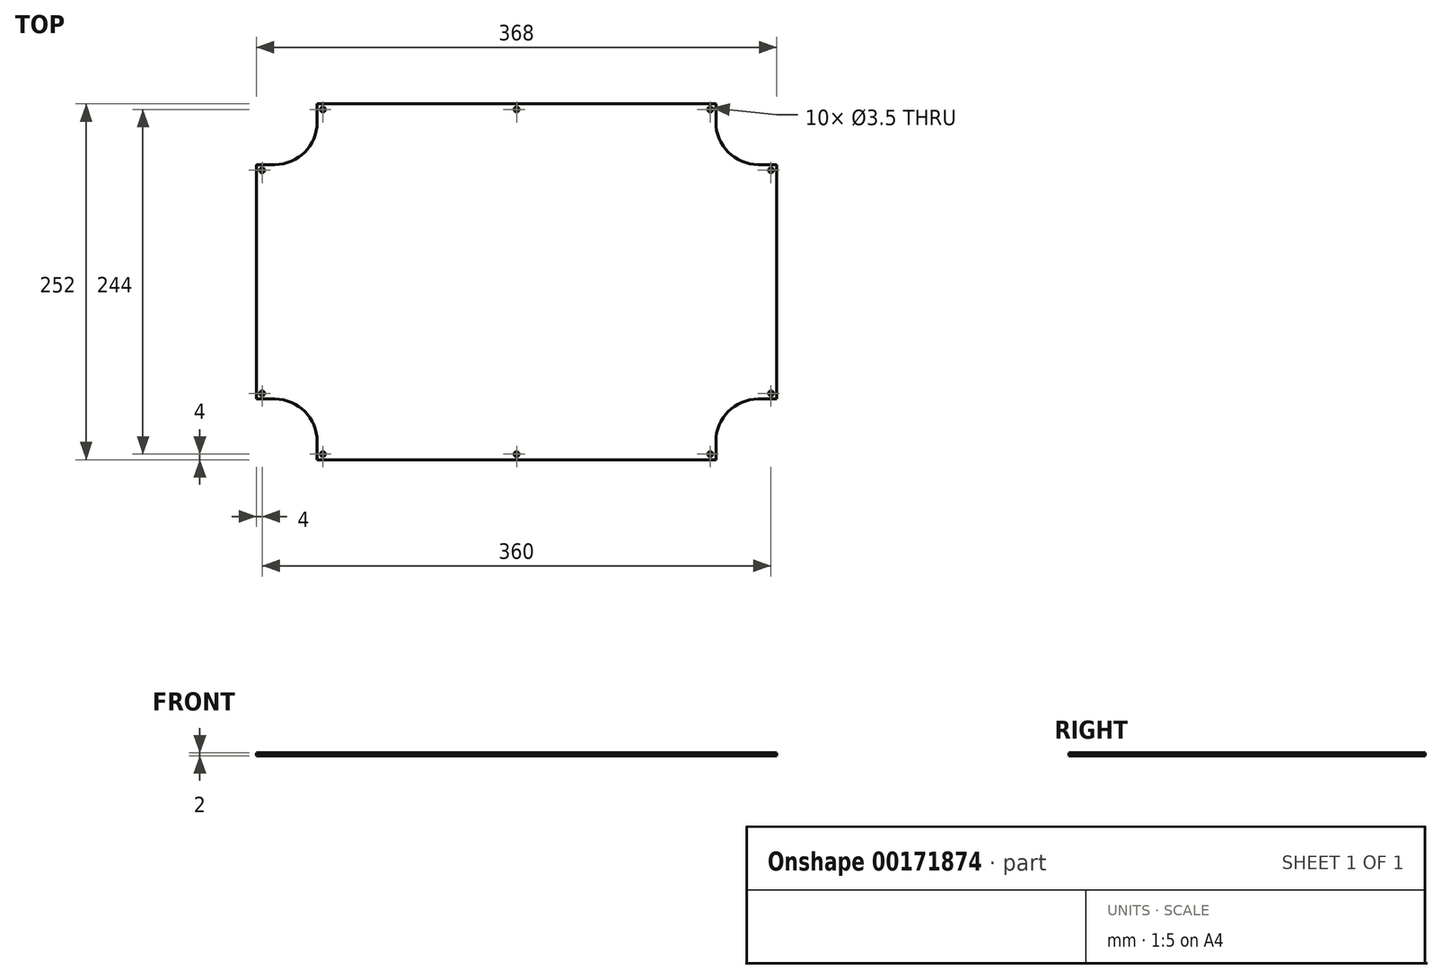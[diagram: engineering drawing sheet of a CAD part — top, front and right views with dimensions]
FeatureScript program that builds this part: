
annotation { "Feature Type Name" : "Feature", "Feature Type Description" : "" }
export const myFeature = defineFeature(function(context is Context, id is Id, definition is map)
    precondition{}
    {
        {
            var Q0;
            Q0=qCreatedBy(makeId("Top.planeOp"),FACE);
            var sketch = newSketch(context, id + "F0", { "sketchPlane" : qUnion([Q0])});
            skLineSegment(sketch, "E0", {"start": v(-141, 126) * mm, "end": v(141, 126) * mm});
            skLineSegment(sketch, "E1", {"start": v(141, 126) * mm, "end": v(141, 113) * mm});
            skLineSegment(sketch, "E2", {"start": v(171, 83) * mm, "end": v(184, 83) * mm});
            skLineSegment(sketch, "E3", {"start": v(184, 83) * mm, "end": v(184, -83) * mm});
            skLineSegment(sketch, "E4", {"start": v(184, -83) * mm, "end": v(171, -83) * mm});
            skLineSegment(sketch, "E5", {"start": v(141, -113) * mm, "end": v(141, -126) * mm});
            skLineSegment(sketch, "E6", {"start": v(141, -126) * mm, "end": v(-141, -126) * mm});
            skLineSegment(sketch, "E7", {"start": v(-141, -126) * mm, "end": v(-141, -113) * mm});
            skLineSegment(sketch, "E8", {"start": v(-171, -83) * mm, "end": v(-184, -83) * mm});
            skLineSegment(sketch, "E9", {"start": v(-184, -83) * mm, "end": v(-184, 83) * mm});
            skLineSegment(sketch, "E10", {"start": v(-184, 83) * mm, "end": v(-171, 83) * mm});
            skLineSegment(sketch, "E11", {"start": v(-141, 113) * mm, "end": v(-141, 126) * mm});
            skPoint(sketch, "E12.visualSharp", {"position": v(-141, 83) * mm});
            skArc(sketch, "E12.filletArc", {"start": v(-171, 83) * mm, "mid": v(-149.79, 91.79) * mm, "end": v(-141, 113) * mm});
            skPoint(sketch, "E13.visualSharp", {"position": v(141, 83) * mm});
            skArc(sketch, "E13.filletArc", {"start": v(141, 113) * mm, "mid": v(149.79, 91.79) * mm, "end": v(171, 83) * mm});
            skPoint(sketch, "E14.visualSharp", {"position": v(141, -83) * mm});
            skArc(sketch, "E14.filletArc", {"start": v(171, -83) * mm, "mid": v(149.79, -91.79) * mm, "end": v(141, -113) * mm});
            skPoint(sketch, "E15.visualSharp", {"position": v(-141, -83) * mm});
            skArc(sketch, "E15.filletArc", {"start": v(-141, -113) * mm, "mid": v(-149.79, -91.79) * mm, "end": v(-171, -83) * mm});
            skPoint(sketch, "E16", {"position": v(0, 126) * mm});
            skPoint(sketch, "E17", {"position": v(0, -126) * mm});
            skPoint(sketch, "E18", {"position": v(-184, 0) * mm});
            skPoint(sketch, "E19", {"position": v(184, 0) * mm});
            skLineSegment(sketch, "E20", {"start": v(-137, 139.15) * mm, "end": v(-137, -174.05) * mm, "construction": true});
            skLineSegment(sketch, "E21", {"start": v(-207.28, 122) * mm, "end": v(169.12, 122) * mm, "construction": true});
            skLineSegment(sketch, "E22", {"start": v(-202.37, 79) * mm, "end": v(209.85, 79) * mm, "construction": true});
            skLineSegment(sketch, "E23.MirrorCS", {"start": v(-202.37, -79) * mm, "end": v(209.85, -79) * mm, "construction": true});
            skLineSegment(sketch, "E24.MirrorCS", {"start": v(-207.28, -122) * mm, "end": v(169.12, -122) * mm, "construction": true});
            skLineSegment(sketch, "E25.MirrorCS", {"start": v(137, 139.15) * mm, "end": v(137, -174.05) * mm, "construction": true});
            skLineSegment(sketch, "E26", {"start": v(-180, 93.5) * mm, "end": v(-180, -106.64) * mm, "construction": true});
            skLineSegment(sketch, "E27.MirrorCS", {"start": v(180, 93.5) * mm, "end": v(180, -106.64) * mm, "construction": true});
            skLineSegment(sketch, "E28", {"start": v(0, 134.08) * mm, "end": v(0, -140) * mm, "construction": true});
            skCircle(sketch, "E29", {"center": v(0, 122) * mm, "radius": 1.75 * mm});
            skCircle(sketch, "E30", {"center": v(-137, 122) * mm, "radius": 1.75 * mm});
            skCircle(sketch, "E31", {"center": v(137, 122) * mm, "radius": 1.75 * mm});
            skCircle(sketch, "E32", {"center": v(-180, 79) * mm, "radius": 1.75 * mm});
            skCircle(sketch, "E33", {"center": v(-180, -79) * mm, "radius": 1.75 * mm});
            skCircle(sketch, "E34", {"center": v(-137, -122) * mm, "radius": 1.75 * mm});
            skCircle(sketch, "E35", {"center": v(0, -122) * mm, "radius": 1.75 * mm});
            skCircle(sketch, "E36", {"center": v(137, -122) * mm, "radius": 1.75 * mm});
            skCircle(sketch, "E37", {"center": v(180, -79) * mm, "radius": 1.75 * mm});
            skCircle(sketch, "E38", {"center": v(180, 79) * mm, "radius": 1.75 * mm});
            skSolve(sketch);
        }
        {
            var Q0;
            Q0=makeQuery(id+"F0.imprint","IMPRINT",FACE,{"disambiguationData":[TD([[makeQuery(id+"F0.imprint","IMPRINT",EDGE,{"derivedFrom":sQuery(id+"F0.wireOp",EDGE,"E0")}),-1.0]])]});
            extrude(context, id + "F1", {"entities" : qUnion([Q0]), "depth" : 2 * mm});
        }
    });
